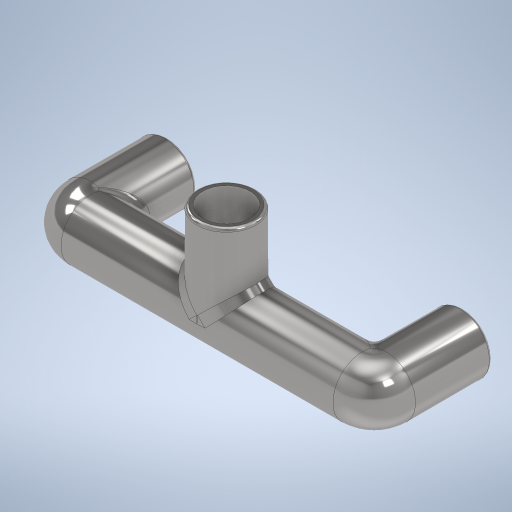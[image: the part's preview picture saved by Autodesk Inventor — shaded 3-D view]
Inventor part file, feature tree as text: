
AUTODESK INVENTOR PART (.ipt)
format: ipt  version: 2024 (Build 280153000, 153)  size: 393,216 bytes
history: native  units: mm
features: sketch x4, fillet x2, sweep x1, plane x1, extrude x1, hole x1, chamfer x1, projected_geometry x1
ambient origin geometry x8: Origin, YZ Plane, XZ Plane, XY Plane, X Axis, Y Axis, Z Axis, Center Point
bodies: Volumenkörper1 (feature_tree)
feature tree (12):
  sweep  "Sweeping1"
  fillet  "Rundung1"  Radius=15.0mm
  plane  "Arbeitsebene3"
  extrude  "Extrusion1"  TaperAngle=0.0deg  [1 undecoded]
  hole  "Bohrung1"  [1 undecoded]
  fillet  "Rundung2"  Radius=15.0mm
  chamfer  "Fasen1"  Distance=10.0mm
  sketch  "Skizze1"  dims[d0=10.0mm d1=25.0mm d2=15.0mm]
  sketch  "Skizze3"  dims[d3=2.0mm d4=0.0mm d5=0.0mm]
  sketch  "Skizze4"  dims[d6=2.0mm d7=7.0mm d8=15.0mm]
  projected_geometry  "Projizierte Kontur1"
  sketch  "Skizze6"  dims[d9=10.0mm d10=10.0mm d11=0.0mm d12=8.0mm d13=6.0mm d14=4.0mm d15=2.0mm d16=90.0deg d17=14.0mm d18=0.0mm d19=0.5mm d20=0.9mm d21=2.0mm d22=45.0deg]
note: 2 required parameter values undecoded (feature->parameter linkage not recoverable at this tier; creation-order binding heuristic only, values carry confidence <= 0.55)
